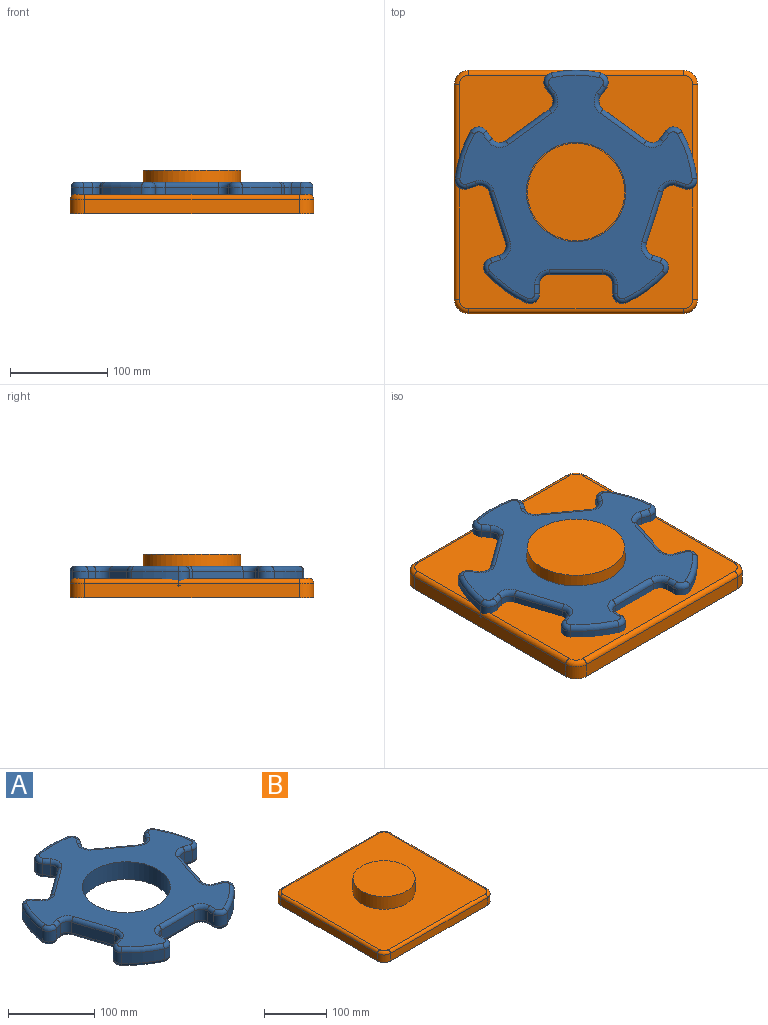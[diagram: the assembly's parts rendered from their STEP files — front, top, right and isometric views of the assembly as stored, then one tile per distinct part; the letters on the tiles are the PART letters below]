
ASSEMBLY  parts=2 mates=1
PART A: 123 faces, bbox 268.9x258.5x25 mm
  f0: plane 238.57x229.73mm, normal (0,0,1), area 21505.7mm2, adj f6,f43,f44,f45,f46,f47,f48,f49
  f1: plane 238.57x229.73mm, normal (0,0,-1), area 21505.7mm2, adj f6,f83,f84,f85,f86,f87,f88,f89
  f2: cylinder r=125mm len=40.68mm, axis (0,0,-1), area 759.5mm2, adj f13,f42,f51,f91
  f3: cylinder r=125mm len=47.82mm, axis (0,0,-1), area 759.5mm2, adj f35,f41,f67,f107
  f4: cylinder r=125mm len=50.29mm, axis (0,0,-1), area 759.5mm2, adj f28,f34,f82,f122
  f5: cylinder r=125mm len=47.82mm, axis (0,0,-1), area 759.5mm2, adj f21,f27,f66,f106
  f6: cylinder r=51mm len=102mm, axis (0,0,-1), area 8011.1mm2, adj f0,f1
  f7: cylinder r=125mm len=40.68mm, axis (0,0,-1), area 759.5mm2, adj f14,f20,f50,f90
  f8: plane 15x9.73mm, normal (-1,0,0), area 146mm2, adj f11,f14,f46,f86
  f9: plane 55x15mm, normal (0,-1,0), area 825mm2, adj f11,f12,f43,f83
  f10: plane 15x9.73mm, normal (1,0,0), area 146mm2, adj f12,f13,f47,f87
  f11: cylinder r=10mm len=15mm, axis (0,0,-1), area 235.6mm2, adj f8,f9,f44,f84
  f12: cylinder r=10mm len=15mm, axis (0,0,-1), area 235.6mm2, adj f9,f10,f45,f85
  f13: cylinder r=10mm len=15mm, axis (0,0,-1), area 299.5mm2, adj f2,f10,f49,f89
  f14: cylinder r=10mm len=15mm, axis (0,0,-1), area 299.5mm2, adj f7,f8,f48,f88
  f15: plane 15x9.26mm, normal (-0.31,-0.95,0), area 146mm2, adj f18,f21,f62,f102
  f16: plane 52.31x17mm, normal (0.95,-0.31,0), area 825mm2, adj f18,f19,f58,f98
  f17: plane 15x9.26mm, normal (0.31,0.95,0), area 146mm2, adj f19,f20,f54,f94
  f18: cylinder r=10mm len=15mm, axis (0,0,-1), area 235.6mm2, adj f15,f16,f60,f100
  f19: cylinder r=10mm len=15mm, axis (0,0,-1), area 235.6mm2, adj f16,f17,f56,f96
  f20: cylinder r=10mm len=16.25mm, axis (0,0,-1), area 299.5mm2, adj f7,f17,f52,f92
  f21: cylinder r=10mm len=15mm, axis (0,0,-1), area 299.5mm2, adj f5,f15,f64,f104
  f22: plane 15x7.87mm, normal (0.81,-0.59,0), area 146mm2, adj f25,f28,f78,f118
  f23: plane 44.5x32.33mm, normal (0.59,0.81,0), area 825mm2, adj f25,f26,f74,f114
  f24: plane 15x7.87mm, normal (-0.81,0.59,0), area 146mm2, adj f26,f27,f70,f110
  f25: cylinder r=10mm len=15mm, axis (0,0,-1), area 235.6mm2, adj f22,f23,f76,f116
  f26: cylinder r=10mm len=15mm, axis (0,0,-1), area 235.6mm2, adj f23,f24,f72,f112
  f27: cylinder r=10mm len=16.78mm, axis (0,0,-1), area 299.5mm2, adj f5,f24,f68,f108
  f28: cylinder r=10mm len=15.67mm, axis (0,0,-1), area 299.5mm2, adj f4,f22,f80,f120
  f29: plane 15x7.87mm, normal (0.81,0.59,0), area 146mm2, adj f32,f35,f71,f111
  f30: plane 44.5x32.33mm, normal (-0.59,0.81,0), area 825mm2, adj f32,f33,f75,f115
  f31: plane 15x7.87mm, normal (-0.81,-0.59,0), area 146mm2, adj f33,f34,f79,f119
  f32: cylinder r=10mm len=15mm, axis (0,0,-1), area 235.6mm2, adj f29,f30,f73,f113
  f33: cylinder r=10mm len=15mm, axis (0,0,-1), area 235.6mm2, adj f30,f31,f77,f117
  f34: cylinder r=10mm len=15.67mm, axis (0,0,-1), area 299.5mm2, adj f4,f31,f81,f121
  f35: cylinder r=10mm len=16.78mm, axis (0,0,-1), area 299.5mm2, adj f3,f29,f69,f109
  f36: plane 15x9.26mm, normal (-0.31,0.95,0), area 146mm2, adj f39,f42,f55,f95
  f37: plane 52.31x17mm, normal (-0.95,-0.31,0), area 825mm2, adj f39,f40,f59,f99
  f38: plane 15x9.26mm, normal (0.31,-0.95,0), area 146mm2, adj f40,f41,f63,f103
  f39: cylinder r=10mm len=15mm, axis (0,0,-1), area 235.6mm2, adj f36,f37,f57,f97
  f40: cylinder r=10mm len=15mm, axis (0,0,-1), area 235.6mm2, adj f37,f38,f61,f101
  f41: cylinder r=10mm len=15mm, axis (0,0,-1), area 299.5mm2, adj f3,f38,f65,f105
  f42: cylinder r=10mm len=16.25mm, axis (0,0,-1), area 299.5mm2, adj f2,f36,f53,f93
  f43: cylinder r=5mm len=55mm, axis (1,0,0), area 432mm2, adj f0,f9,f44,f45
  f44: torus R=15mm, axis (0,0,1), area 145.8mm2, adj f0,f11,f43,f46
  f45: torus R=15mm, axis (0,0,1), area 145.8mm2, adj f0,f12,f43,f47
  f46: cylinder r=5mm len=9.73mm, axis (0,-1,0), area 76.4mm2, adj f0,f8,f44,f48
  f47: cylinder r=5mm len=9.73mm, axis (0,1,0), area 76.4mm2, adj f0,f10,f45,f49
  f48: torus R=5mm, axis (0,0,1), area 128.3mm2, adj f0,f14,f46,f50
  f49: torus R=5mm, axis (0,0,1), area 128.3mm2, adj f0,f13,f47,f51
  f50: torus R=120mm, axis (0,0,1), area 391.9mm2, adj f0,f7,f48,f52
  f51: torus R=120mm, axis (0,0,1), area 391.9mm2, adj f0,f2,f49,f53
  f52: torus R=5mm, axis (0,0,1), area 128.3mm2, adj f0,f20,f50,f54
  f53: torus R=5mm, axis (0,0,1), area 128.3mm2, adj f0,f42,f51,f55
  f54: cylinder r=5mm len=10.8mm, axis (-0.95,0.31,0), area 76.4mm2, adj f0,f17,f52,f56
  f55: cylinder r=5mm len=10.8mm, axis (-0.95,-0.31,0), area 76.4mm2, adj f0,f36,f53,f57
  f56: torus R=15mm, axis (0,0,1), area 145.8mm2, adj f0,f19,f54,f58
  f57: torus R=15mm, axis (0,0,1), area 145.8mm2, adj f0,f39,f55,f59
  f58: cylinder r=5mm len=53.85mm, axis (0.31,0.95,0), area 432mm2, adj f0,f16,f56,f60
  f59: cylinder r=5mm len=53.85mm, axis (0.31,-0.95,0), area 432mm2, adj f0,f37,f57,f61
  f60: torus R=15mm, axis (0,0,1), area 145.8mm2, adj f0,f18,f58,f62
  f61: torus R=15mm, axis (0,0,1), area 145.8mm2, adj f0,f40,f59,f63
  f62: cylinder r=5mm len=10.8mm, axis (0.95,-0.31,0), area 76.4mm2, adj f0,f15,f60,f64
  f63: cylinder r=5mm len=10.8mm, axis (0.95,0.31,0), area 76.4mm2, adj f0,f38,f61,f65
  f64: torus R=5mm, axis (0,0,1), area 128.3mm2, adj f0,f21,f62,f66
  f65: torus R=5mm, axis (0,0,1), area 128.3mm2, adj f0,f41,f63,f67
  f66: torus R=120mm, axis (0,0,1), area 391.9mm2, adj f0,f5,f64,f68
  f67: torus R=120mm, axis (0,0,1), area 391.9mm2, adj f0,f3,f65,f69
  f68: torus R=5mm, axis (0,0,1), area 128.3mm2, adj f0,f27,f66,f70
  f69: torus R=5mm, axis (0,0,1), area 128.3mm2, adj f0,f35,f67,f71
  f70: cylinder r=5mm len=10.81mm, axis (-0.59,-0.81,0), area 76.4mm2, adj f0,f24,f68,f72
  f71: cylinder r=5mm len=10.81mm, axis (-0.59,0.81,0), area 76.4mm2, adj f0,f29,f69,f73
  f72: torus R=15mm, axis (0,0,1), area 145.8mm2, adj f0,f26,f70,f74
  f73: torus R=15mm, axis (0,0,1), area 145.8mm2, adj f0,f32,f71,f75
  f74: cylinder r=5mm len=47.44mm, axis (-0.81,0.59,0), area 432mm2, adj f0,f23,f72,f76
  f75: cylinder r=5mm len=47.44mm, axis (-0.81,-0.59,0), area 432mm2, adj f0,f30,f73,f77
  f76: torus R=15mm, axis (0,0,1), area 145.8mm2, adj f0,f25,f74,f78
  f77: torus R=15mm, axis (0,0,1), area 145.8mm2, adj f0,f33,f75,f79
  f78: cylinder r=5mm len=10.81mm, axis (0.59,0.81,0), area 76.4mm2, adj f0,f22,f76,f80
  f79: cylinder r=5mm len=10.81mm, axis (0.59,-0.81,0), area 76.4mm2, adj f0,f31,f77,f81
  f80: torus R=5mm, axis (0,0,1), area 128.3mm2, adj f0,f28,f78,f82
  f81: torus R=5mm, axis (0,0,1), area 128.3mm2, adj f0,f34,f79,f82
  f82: torus R=120mm, axis (0,0,1), area 391.9mm2, adj f0,f4,f80,f81
  f83: cylinder r=5mm len=55mm, axis (-1,0,0), area 432mm2, adj f1,f9,f84,f85
  f84: torus R=15mm, axis (0,0,1), area 145.8mm2, adj f1,f11,f83,f86
  f85: torus R=15mm, axis (0,0,1), area 145.8mm2, adj f1,f12,f83,f87
  f86: cylinder r=5mm len=9.73mm, axis (0,1,0), area 76.4mm2, adj f1,f8,f84,f88
  f87: cylinder r=5mm len=9.73mm, axis (0,-1,0), area 76.4mm2, adj f1,f10,f85,f89
  f88: torus R=5mm, axis (0,0,1), area 128.3mm2, adj f1,f14,f86,f90
  f89: torus R=5mm, axis (0,0,1), area 128.3mm2, adj f1,f13,f87,f91
  f90: torus R=120mm, axis (0,0,1), area 391.9mm2, adj f1,f7,f88,f92
  f91: torus R=120mm, axis (0,0,1), area 391.9mm2, adj f1,f2,f89,f93
  f92: torus R=5mm, axis (0,0,1), area 128.3mm2, adj f1,f20,f90,f94
  f93: torus R=5mm, axis (0,0,1), area 128.3mm2, adj f1,f42,f91,f95
  f94: cylinder r=5mm len=10.8mm, axis (0.95,-0.31,0), area 76.4mm2, adj f1,f17,f92,f96
  f95: cylinder r=5mm len=10.8mm, axis (0.95,0.31,0), area 76.4mm2, adj f1,f36,f93,f97
  f96: torus R=15mm, axis (0,0,1), area 145.8mm2, adj f1,f19,f94,f98
  f97: torus R=15mm, axis (0,0,1), area 145.8mm2, adj f1,f39,f95,f99
  f98: cylinder r=5mm len=53.85mm, axis (-0.31,-0.95,0), area 432mm2, adj f1,f16,f96,f100
  f99: cylinder r=5mm len=53.85mm, axis (-0.31,0.95,0), area 432mm2, adj f1,f37,f97,f101
  f100: torus R=15mm, axis (0,0,1), area 145.8mm2, adj f1,f18,f98,f102
  f101: torus R=15mm, axis (0,0,1), area 145.8mm2, adj f1,f40,f99,f103
  f102: cylinder r=5mm len=10.8mm, axis (-0.95,0.31,0), area 76.4mm2, adj f1,f15,f100,f104
  f103: cylinder r=5mm len=10.8mm, axis (-0.95,-0.31,0), area 76.4mm2, adj f1,f38,f101,f105
  f104: torus R=5mm, axis (0,0,1), area 128.3mm2, adj f1,f21,f102,f106
  f105: torus R=5mm, axis (0,0,1), area 128.3mm2, adj f1,f41,f103,f107
  f106: torus R=120mm, axis (0,0,1), area 391.9mm2, adj f1,f5,f104,f108
  f107: torus R=120mm, axis (0,0,1), area 391.9mm2, adj f1,f3,f105,f109
  f108: torus R=5mm, axis (0,0,1), area 128.3mm2, adj f1,f27,f106,f110
  f109: torus R=5mm, axis (0,0,1), area 128.3mm2, adj f1,f35,f107,f111
  f110: cylinder r=5mm len=10.81mm, axis (0.59,0.81,0), area 76.4mm2, adj f1,f24,f108,f112
  f111: cylinder r=5mm len=10.81mm, axis (0.59,-0.81,0), area 76.4mm2, adj f1,f29,f109,f113
  f112: torus R=15mm, axis (0,0,1), area 145.8mm2, adj f1,f26,f110,f114
  f113: torus R=15mm, axis (0,0,1), area 145.8mm2, adj f1,f32,f111,f115
  f114: cylinder r=5mm len=47.44mm, axis (0.81,-0.59,0), area 432mm2, adj f1,f23,f112,f116
  f115: cylinder r=5mm len=47.44mm, axis (0.81,0.59,0), area 432mm2, adj f1,f30,f113,f117
  f116: torus R=15mm, axis (0,0,1), area 145.8mm2, adj f1,f25,f114,f118
  f117: torus R=15mm, axis (0,0,1), area 145.8mm2, adj f1,f33,f115,f119
  f118: cylinder r=5mm len=10.81mm, axis (-0.59,-0.81,0), area 76.4mm2, adj f1,f22,f116,f120
  f119: cylinder r=5mm len=10.81mm, axis (-0.59,0.81,0), area 76.4mm2, adj f1,f31,f117,f121
  f120: torus R=5mm, axis (0,0,1), area 128.3mm2, adj f1,f28,f118,f122
  f121: torus R=5mm, axis (0,0,1), area 128.3mm2, adj f1,f34,f119,f122
  f122: torus R=120mm, axis (0,0,1), area 391.9mm2, adj f1,f4,f120,f121
PART B: 20 faces, bbox 252.5x252.5x45 mm
  f0: plane 220x15mm, normal (1,0,0), area 3300mm2, adj f5,f8,f11,f15
  f1: plane 220x15mm, normal (0,1,0), area 3300mm2, adj f5,f8,f9,f19
  f2: plane 220x15mm, normal (-1,0,0), area 3300mm2, adj f5,f9,f10,f16
  f3: plane 220x15mm, normal (0,-1,0), area 3300mm2, adj f5,f10,f11,f12
  f4: plane 240x240mm, normal (0,0,1), area 49660.2mm2, adj f6,f12,f13,f14,f15,f16,f17,f18
  f5: plane 250x250mm, normal (0,0,-1), area 62306.9mm2, adj f0,f1,f2,f3,f8,f9,f10,f11
  f6: cylinder r=50mm len=100mm, axis (0,0,-1), area 7854mm2, adj f4,f7
  f7: plane 100x100mm, normal (0,0,1), area 7854mm2, adj f6
  f8: cylinder r=15mm len=15mm, axis (0,0,-1), area 353.4mm2, adj f0,f1,f5,f17
  f9: cylinder r=15mm len=15mm, axis (0,0,1), area 353.4mm2, adj f1,f2,f5,f18
  f10: cylinder r=15mm len=15mm, axis (0,0,-1), area 353.4mm2, adj f2,f3,f5,f14
  f11: cylinder r=15mm len=15mm, axis (0,0,1), area 353.4mm2, adj f0,f3,f5,f13
  f12: cylinder r=5mm len=220mm, axis (-1,0,0), area 1727.9mm2, adj f3,f4,f13,f14
  f13: torus R=10mm, axis (0,0,1), area 162.6mm2, adj f4,f11,f12,f15
  f14: torus R=10mm, axis (0,0,1), area 162.6mm2, adj f4,f10,f12,f16
  f15: cylinder r=5mm len=220mm, axis (0,-1,0), area 1727.9mm2, adj f0,f4,f13,f17
  f16: cylinder r=5mm len=220mm, axis (0,1,0), area 1727.9mm2, adj f2,f4,f14,f18
  f17: torus R=10mm, axis (0,0,1), area 162.6mm2, adj f4,f8,f15,f19
  f18: torus R=10mm, axis (0,0,1), area 162.6mm2, adj f4,f9,f16,f19
  f19: cylinder r=5mm len=220mm, axis (1,0,0), area 1727.9mm2, adj f1,f4,f17,f18
PLACE A t=(0,0,-12.5)mm
PLACE B at identity
MATE revolute A.f2 <-> B.f6  axis (0,0,-1) through (0,0,20)mm
